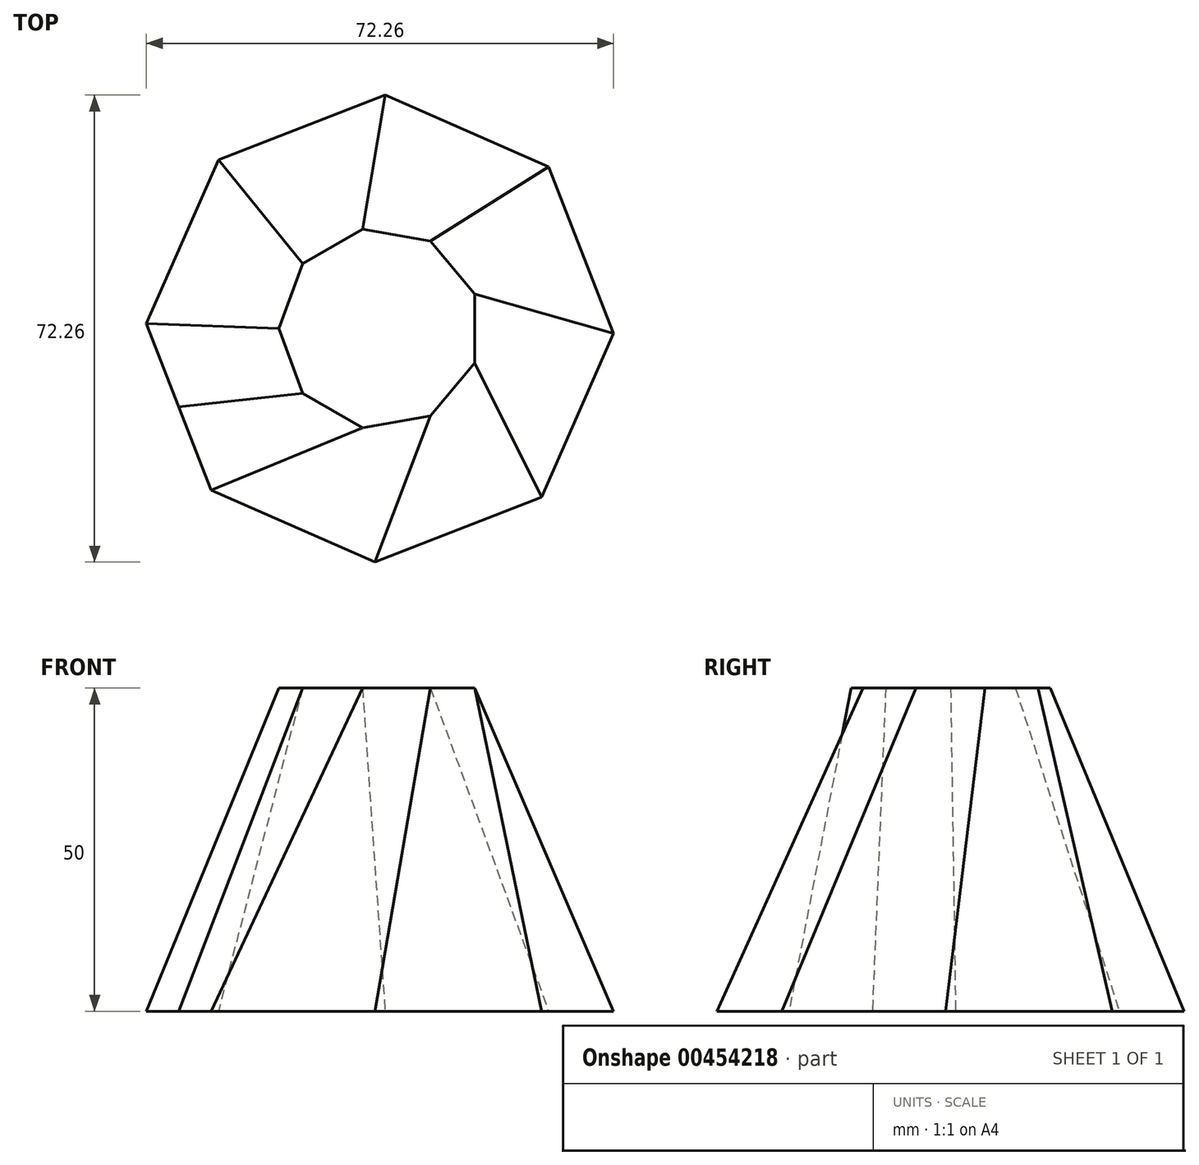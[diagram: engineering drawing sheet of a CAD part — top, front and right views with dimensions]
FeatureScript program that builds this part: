
annotation { "Feature Type Name" : "Feature", "Feature Type Description" : "" }
export const myFeature = defineFeature(function(context is Context, id is Id, definition is map)
    precondition{}
    {
        {
            var Q0;
            Q0=qCreatedBy(makeId("Top.planeOp"),FACE);
            var sketch = newSketch(context, id + "F0", { "sketchPlane" : qUnion([Q0])});
            skCircle(sketch, "E0.cCircle", {"center": v(0, 0) * mm, "radius": 33.4 * mm, "construction": true});
            skLineSegment(sketch, "E0.0", {"start": v(25, -26.1) * mm, "end": v(-0.78, -36.13) * mm});
            skLineSegment(sketch, "E0.1", {"start": v(-0.78, -36.13) * mm, "end": v(-26.1, -25) * mm});
            skLineSegment(sketch, "E0.2", {"start": v(-26.1, -25) * mm, "end": v(-36.13, 0.78) * mm});
            skLineSegment(sketch, "E0.3", {"start": v(-36.13, 0.78) * mm, "end": v(-25, 26.1) * mm});
            skLineSegment(sketch, "E0.4", {"start": v(-25, 26.1) * mm, "end": v(0.78, 36.13) * mm});
            skLineSegment(sketch, "E0.5", {"start": v(0.78, 36.13) * mm, "end": v(26.1, 25) * mm});
            skLineSegment(sketch, "E0.6", {"start": v(26.1, 25) * mm, "end": v(36.13, -0.78) * mm});
            skLineSegment(sketch, "E0.7", {"start": v(36.13, -0.78) * mm, "end": v(25, -26.1) * mm});
            skPoint(sketch, "E0.0.midPoint", {"position": v(12.1, -31.12) * mm});
            skSolve(sketch);
        }
        {
            var Q0;
            Q0=qCreatedBy(makeId("Top.planeOp"),FACE);
            cPlane(context, id + "F1", {"entities" : qUnion([Q0]), "cplaneType" : CPlaneType.OFFSET, "offset" : 50 * mm, "width" : 150 * mm, "height" : 150 * mm});
        }
        {
            var Q0;
            Q0=qCreatedBy(id+"F1.planeOp",FACE);
            var sketch = newSketch(context, id + "F2", { "sketchPlane" : qUnion([Q0])});
            skCircle(sketch, "E1.cCircle", {"center": v(0, 0) * mm, "radius": 14.68 * mm, "construction": true});
            skLineSegment(sketch, "E1.0", {"start": v(14.68, 5.34) * mm, "end": v(14.68, -5.34) * mm});
            skLineSegment(sketch, "E1.1", {"start": v(14.68, -5.34) * mm, "end": v(7.81, -13.53) * mm});
            skLineSegment(sketch, "E1.2", {"start": v(7.81, -13.53) * mm, "end": v(-2.71, -15.39) * mm});
            skLineSegment(sketch, "E1.3", {"start": v(-2.71, -15.39) * mm, "end": v(-11.97, -10.04) * mm});
            skLineSegment(sketch, "E1.4", {"start": v(-11.97, -10.04) * mm, "end": v(-15.62, 0) * mm});
            skLineSegment(sketch, "E1.5", {"start": v(-15.62, 0) * mm, "end": v(-11.97, 10.04) * mm});
            skLineSegment(sketch, "E1.6", {"start": v(-11.97, 10.04) * mm, "end": v(-2.71, 15.39) * mm});
            skLineSegment(sketch, "E1.7", {"start": v(-2.71, 15.39) * mm, "end": v(7.81, 13.53) * mm});
            skLineSegment(sketch, "E1.8", {"start": v(7.81, 13.53) * mm, "end": v(14.68, 5.34) * mm});
            skPoint(sketch, "E1.0.midPoint", {"position": v(14.68, 0) * mm});
            skSolve(sketch);
        }
        {
            var Q0;
            Q0 = qSketchRegion(id + "F2", true);
            var Q1;
            Q1 = qSketchRegion(id + "F0", true);
            loft(context, id + "F3", {"sheetProfilesArray" : [{ "sheetProfileEntities" : qUnion([Q0]) }, { "sheetProfileEntities" : qUnion([Q1]) }]});
        }
    });
